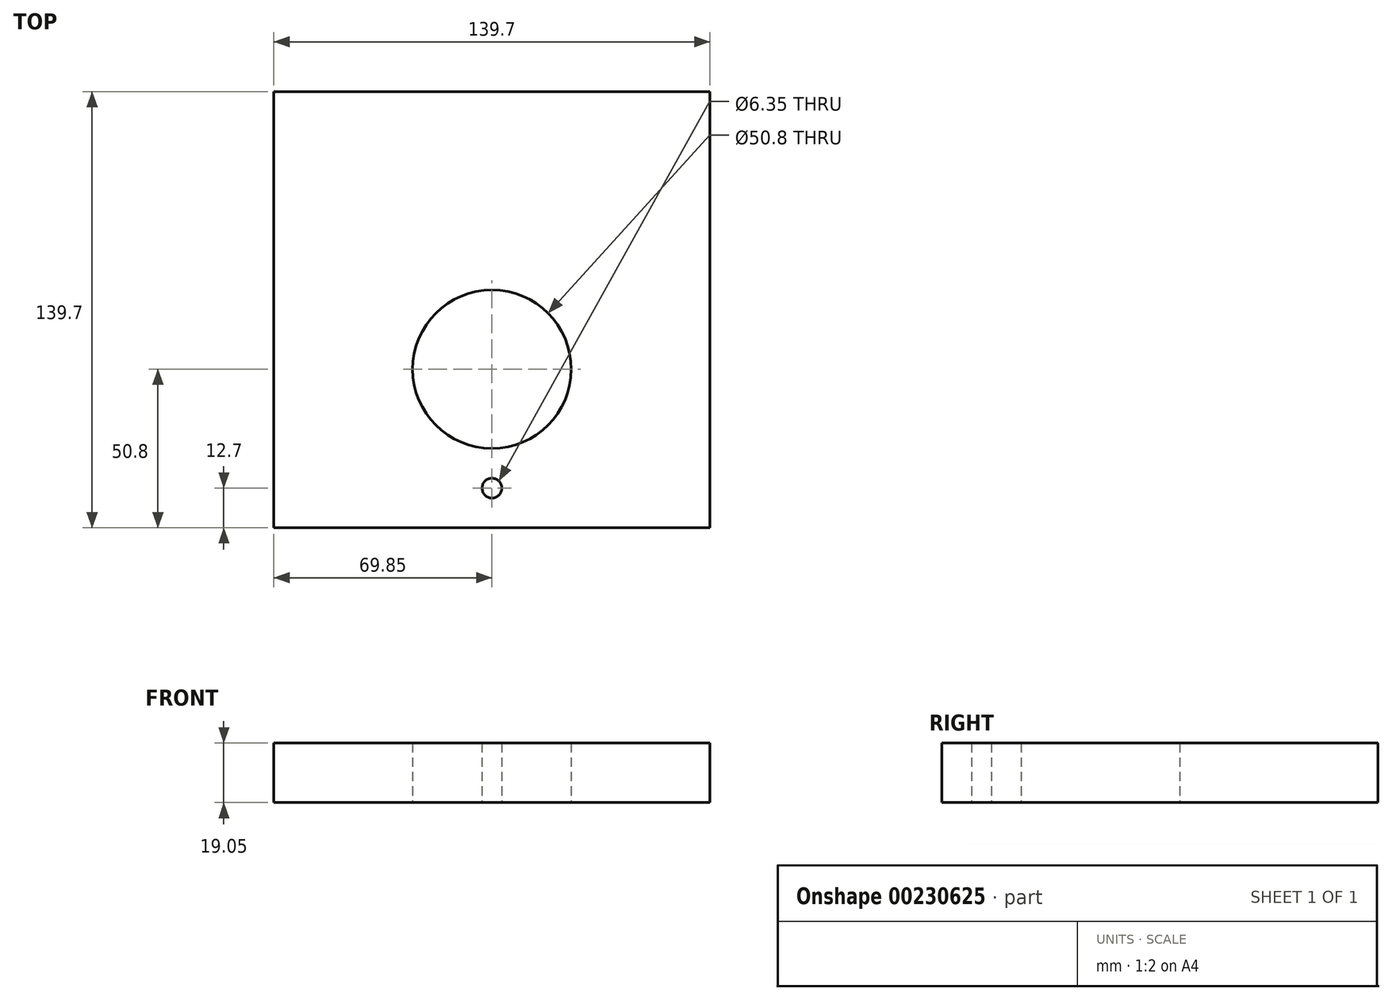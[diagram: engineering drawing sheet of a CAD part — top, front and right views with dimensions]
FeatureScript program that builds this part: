
annotation { "Feature Type Name" : "Feature", "Feature Type Description" : "" }
export const myFeature = defineFeature(function(context is Context, id is Id, definition is map)
    precondition{}
    {
        {
            var Q0;
            Q0=qCreatedBy(makeId("Top.planeOp"),FACE);
            var sketch = newSketch(context, id + "F0", { "sketchPlane" : qUnion([Q0])});
            skLineSegment(sketch, "E0.bottom", {"start": v(69.85, 69.85) * mm, "end": v(-69.85, 69.85) * mm});
            skLineSegment(sketch, "E0.top", {"start": v(69.85, -69.85) * mm, "end": v(-69.85, -69.85) * mm});
            skLineSegment(sketch, "E0.left", {"start": v(69.85, 69.85) * mm, "end": v(69.85, -69.85) * mm});
            skLineSegment(sketch, "E0.right", {"start": v(-69.85, 69.85) * mm, "end": v(-69.85, -69.85) * mm});
            skPoint(sketch, "E0.middle", {"position": v(0, 0) * mm});
            skLineSegment(sketch, "E1", {"start": v(0, -69.85) * mm, "end": v(0, -57.15) * mm});
            skPoint(sketch, "E1.endSnap0", {"position": v(0, -69.85) * mm});
            skLineSegment(sketch, "E2", {"start": v(0, -57.15) * mm, "end": v(0, -19.05) * mm});
            skCircle(sketch, "E3", {"center": v(0, -19.05) * mm, "radius": 25.4 * mm});
            skCircle(sketch, "E4", {"center": v(0, -57.15) * mm, "radius": 3.18 * mm});
            skSolve(sketch);
        }
        {
            var Q0;
            Q0=makeQuery(id+"F0.imprint","IMPRINT",FACE,{"disambiguationData":[TD([[makeQuery(id+"F0.imprint","IMPRINT",EDGE,{"derivedFrom":sQuery(id+"F0.wireOp",EDGE,"E0.bottom")}),1.0]])]});
            extrude(context, id + "F1", {"entities" : qUnion([Q0]), "depth" : 19.05 * mm});
        }
    });
